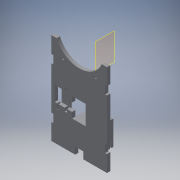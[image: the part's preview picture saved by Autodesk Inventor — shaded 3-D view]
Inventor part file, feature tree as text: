
AUTODESK INVENTOR PART (.ipt)
format: ipt  version: 2016 (Build 200138000, 138)  size: 310,784 bytes
history: native  units: in
note: dims shown in document units (in); Inventor stores cm internally (conversion verified against a paired STEP export)
features: reference x18, extrude x13, sketch x12, plane x2
ambient origin geometry x8: Origin, YZ Plane, XZ Plane, XY Plane, X Axis, Y Axis, Z Axis, Center Point
bodies: Solid1 (feature_tree)
feature tree (45):
  extrude  "Extrusion1"  Depth=0.1969in TaperAngle=0.0deg
  extrude  "Extrusion2"  Depth=0.1969in TaperAngle=0.0deg
  extrude  "Extrusion3"  Depth=0.0787in
  extrude  "Extrusion4"  Depth=0.1969in TaperAngle=0.0deg
  extrude  "Extrusion6"  Depth=0.1969in
  extrude  "Extrusion7"  Depth=0.1969in TaperAngle=0.0deg
  extrude  "Extrusion8"  Depth=0.5in
  plane  "Work Plane1"
  extrude  "Extrusion18"  Depth=0.25in TaperAngle=0.0deg
  extrude  "Extrusion19"  Depth=0.15in
  extrude  "Extrusion21"  Depth=0.1181in
  plane  "Work Plane2"
  extrude  "Extrusion23"  Depth=1.0in TaperAngle=0.0deg
  extrude  "Extrusion24"  Depth=0.325in
  extrude  "Extrusion25"  Depth=0.3937in
  sketch  "Sketch1"  dims[d0=6.0in d1=0.1969in d2=0.0in]
  sketch  "Sketch2"  dims[d3=0.5906in d4=0.1969in d5=0.0in]
  reference  "Reference2"
  reference  "Reference3"
  sketch  "Sketch4"  dims[d6=3.0in d7=0.0787in]
  sketch  "Sketch6"  dims[d8=0.0787in d9=0.1969in d10=0.0in]
  sketch  "Sketch7"  dims[d11=0.1969in d12=0.1969in]
  sketch  "Sketch8"  dims[d13=0.1969in d14=0.1969in d15=0.0in]
  reference  "Reference6"
  reference  "Reference7"
  reference  "Reference8"
  reference  "Reference9"
  reference  "Reference10"
  reference  "Reference11"
  reference  "Reference12"
  reference  "Reference13"
  reference  "Reference14"
  reference  "Reference15"
  sketch  "Sketch18"  dims[d18=0.25in d19=0.5in]
  sketch  "Sketch20"  dims[d20=0.4in d21=0.0in d24=0.25in d25=0.0in]
  sketch  "Sketch22"  dims[d26=0.15in d27=0.1378in]
  sketch  "Sketch24"  dims[d28=0.0394in d29=0.1181in]
  reference  "Reference31"
  sketch  "Sketch25"  dims[d30=0.0394in d31=1.0in d32=0.0in]
  reference  "Reference32"
  reference  "Reference33"
  reference  "Reference34"
  sketch  "Sketch26"  dims[d33=0.02in d34=0.325in d35=0.02in d45=0.0197in d46=0.0197in d47=0.0197in d73=0.1181in d83=1.0in d84=0.5in d85=0.118in d86=1.0in d87=0.5in d88=0.118in d89=0.3937in d90=0.0in d91=0.8226in d92=0.0in d95=0.1in d96=0.0in d102=0.7in d103=1.063in d104=1.5in d106=0.7268in d107=0.8in d108=0.118in d109=0.5in d110=0.1in d111=1.2614in d112=0.0in d113=0.18in d114=0.18in d115=0.8in d116=0.3937in d117=0.0in d118=0.1181in d119=0.1181in d120=0.3937in d121=0.0in]
  reference  "Reference35"
  reference  "Reference36"
